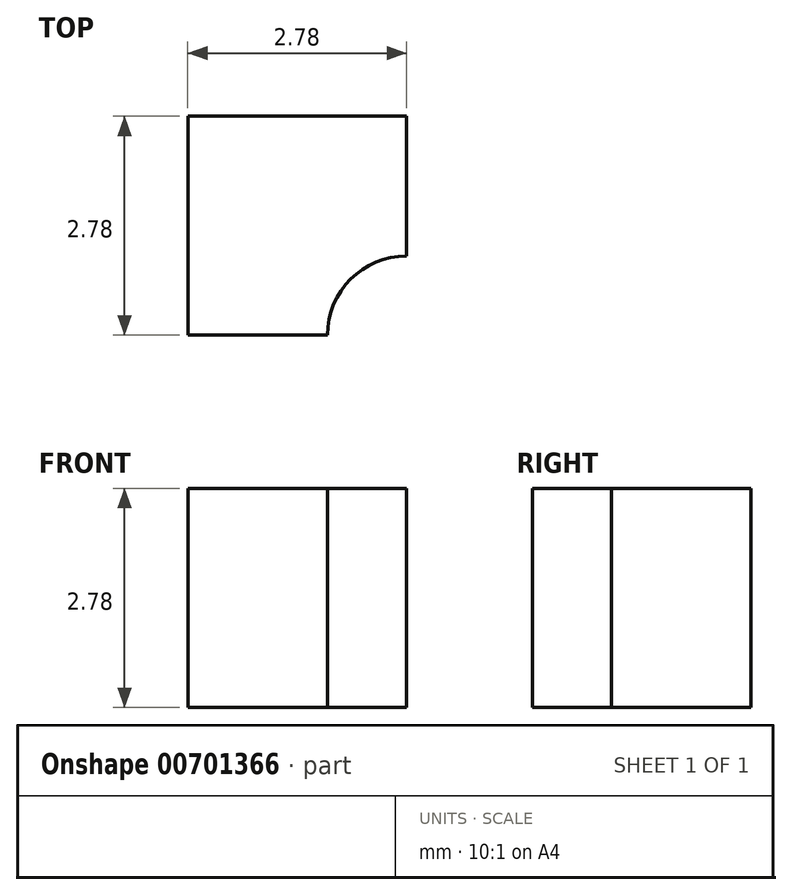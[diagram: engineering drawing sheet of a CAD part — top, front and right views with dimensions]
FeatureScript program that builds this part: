
annotation { "Feature Type Name" : "Feature", "Feature Type Description" : "" }
export const myFeature = defineFeature(function(context is Context, id is Id, definition is map)
    precondition{}
    {
        {
            var Q0;
            Q0=qCreatedBy(makeId("Top.planeOp"),FACE);
            var sketch = newSketch(context, id + "F0", { "sketchPlane" : qUnion([Q0])});
            skLineSegment(sketch, "E0.bottom", {"start": v(0, 0) * mm, "end": v(-2.78, 0) * mm});
            skLineSegment(sketch, "E0.top", {"start": v(0, 2.78) * mm, "end": v(-2.78, 2.78) * mm});
            skLineSegment(sketch, "E0.left", {"start": v(0, 0) * mm, "end": v(0, 2.78) * mm});
            skLineSegment(sketch, "E0.right", {"start": v(-2.78, 0) * mm, "end": v(-2.78, 2.78) * mm});
            skCircle(sketch, "E1", {"center": v(0, 0) * mm, "radius": 1 * mm});
            skSolve(sketch);
        }
        {
            var Q0;
            {var subQ2=sQuery(id+"F0.wireOp",EDGE,"E0.top");Q0=makeQuery(id+"F0.imprint","IMPRINT",FACE,{"disambiguationData":[TD([[makeQuery(id+"F0.imprint","IMPRINT",EDGE,{"derivedFrom":subQ2}),1.0]])]});}
            extrude(context, id + "F1", {"entities" : qUnion([Q0]), "depth" : 2.78 * mm, "offsetDistance" : 25.4 * mm});
        }
    });
